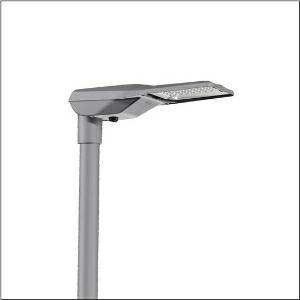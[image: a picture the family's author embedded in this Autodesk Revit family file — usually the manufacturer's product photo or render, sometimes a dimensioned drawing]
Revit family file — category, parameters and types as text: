
# Revit family: streetlight_sl_21_mini___st1_0ab_5xe2m33r08gb_46d4
name_source: partatom
category: Lighting Fixtures
units: mm (PartAtom-declared; Revit-internal decimal feet)

## family parameters
Cut with Voids When Loaded = No
Host = Face
Light Source = No
Part Type = Normal
Room Calculation Point = No
Round Connector Dimension = Use Diameter
Shared = No

## types (1)
- --- (1 x LED, 5230 lm, 40.4 W, 3000K)
    Apparent Load = 40 VA
    CIE Flux Codes = 38 73 97 100 100
    Color Rendering = 70
    Color Temperature = 3000K
    Default Elevation = 1800 mm
    Description = Streetlight SL 21 mini, mast luminaire, primary light control with lens, of PMMA, primary optical cover: cover, of toughened safety glass, transparent, light distribution: ST1.0aB, light emission: direct distribution, primary light characteristic: asymmetric, installation type: side-entry, post-top, LED, High Power LED, rated luminous flux: 5.230lm, luminous efficacy: 130lm/W, light colour: 730, colour temperature: 3000K, control gear: D4i, control: flexible luminous flux parameterisation, time-dependent luminous flux control, constant luminous flux control, overheat protection, pre-setting: logarithmic dimming characteristic, mains connection: 220..240V, AC, 50/60Hz, start of lifetime: 40W, end of service life: 41W, reduction: 19W, luminaire housing, of diecast aluminium, powder-coated, SITECO metallic grey (DB 702S), corrosivity category C5 high according to DIN EN ISO 12944, please order mast flange separately, inclination adjustable: 0°, 5°, 10°, 15°, sealing non-destructively replaceable, multi-level sealing system, length: 628mm, width: 235mm, height: 110mm, mast flange for spigot size: 42mm (side-entry): 5XC10008XM4, 60/48mm (side-entry/post-top): 5XC10108XM2, 76/60mm (side-entry/post-top): 5XC10108XM1, mounting height: 4..8m, Smart Interface below, protection rating (complete): IP66, insulation class (complete): insulation class II (safety insulation), certification: CE, ENEC, ENEC+, VDE, impact resistance: IK10, permissible operating ambient temperature for outdoor applications: -40..+50°C, standard-compliant lighting for roads and squares, packaging unit: 1 piece

Light Distribution: ST1.0aB
    Height = 110 mm
    Lamp = 1 x LED
    Lamp Light Flux = 5230 lm
    Lamp Power = 40.4 W
    Lamp count = 1
    Length = 625 mm
    Luminous efficacy = 129 lm/W
    Manufacturer = Siteco
    ModVariant = No
    Model = 5XE2M33R08GB
    Number of Poles = 1
    OnlyDefault = Yes
    Power Factor = 1
    Product Name = Streetlight SL 21 mini | ST1.0aB
    Product group = mast luminaire | pylon top
    ProductGroupID = 6100
    Protection Class = Protection class II
    Protection Degree = IP 66
    RLX_Detail_Level = 1
    RLX_Emergency_Light_Flux = 0 lm
    RLX_Emergency_Type = 0
    RLX_Emergency_Type_DB = No
    RlxData = <blob elided: 26313 chars, md5=973134b8>
    Socket = socket
    Standby Power = 0 W
    System Light Flux = 5230 lm
    System Power = 40 W
    Type Comments = factory setting: luminous flux: 100 % | dim-lin: 254 | 812 mA
    Type Image = l_1003516.jpg
    URL = http://relux.com
    VarID = @adj_180155
    Voltage = 0 V
    Weight = 0.00 kg
    Width = 234 mm

## geometry (parser evidence)
native form markers: Blend x4, Sweep x9
no freeform markers — native parametric forms only
